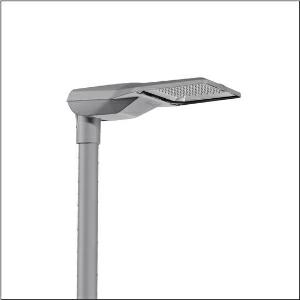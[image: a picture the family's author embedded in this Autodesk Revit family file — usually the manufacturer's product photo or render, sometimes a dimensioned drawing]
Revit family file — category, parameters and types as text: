
# Revit family: streetlight_sl_21_midi___st1_0a_5xe7d33a08nb_63de
name_source: partatom
category: Lighting Fixtures
units: mm (PartAtom-declared; Revit-internal decimal feet)

## family parameters
Cut with Voids When Loaded = No
Host = Face
Light Source = No
Part Type = Normal
Room Calculation Point = No
Round Connector Dimension = Use Diameter
Shared = No

## types (1)
- --- (1 x LED, 22700 lm, 151.2 W, 3000K)
    Apparent Load = 151 VA
    CIE Flux Codes = 40 73 97 100 100
    Color Rendering = 70
    Color Temperature = 3000K
    Default Elevation = 1800 mm
    Description = Streetlight SL 21 midi, mast luminaire, primary light control with lens, of PMMA, primary optical cover: cover, of toughened safety glass, transparent, light distribution: ST1.0a, light emission: direct distribution, primary light characteristic: asymmetric, installation type: post-top, side-entry, LED, 3G 1.5mm², High Power LED, rated luminous flux: 22.700lm, luminous efficacy: 150lm/W, light colour: 730, colour temperature: 3000K, control: flexible luminous flux parameterisation, time-dependent luminous flux control, constant luminous flux control, overheat protection, mains connection: 220..240V, AC, 50/60Hz, connection cable pre-assembled, cable length: 12,5m, wiring characteristics: H07RN-F, start of lifetime: 151W, end of service life: 157W, reduction: 70W, luminaire housing, of diecast aluminium, powder-coated, Siteco® metallic grey (DB 702S), corrosivity category C5 mid according to DIN EN ISO 12944, please order mast flange separately, inclination adjustable: 0°, 5°, 10°, 15°, sealing non-destructively replaceable, multi-level sealing system, length: 644mm, width: 335mm, height: 110mm, mast flange for spigot size: 42mm (side-entry): 5XC10008XM4, 60/48mm (side-entry/post-top): 5XC10108XM2, 76/60mm (side-entry/post-top): 5XC10108XM1, protection rating (complete): IP66, insulation class (complete): insulation class II (safety insulation), certification: CE, ENEC, ENEC+, VDE, impact resistance: IK09, permissible operating ambient temperature for outdoor applications: -40..+50°C, standard-compliant lighting for roads and squares, packaging unit: 1 piece

Light Distribution: ST1.0a
    Height = 111 mm
    Lamp = 1 x LED
    Lamp Light Flux = 22700 lm
    Lamp Power = 151.2 W
    Lamp count = 1
    Length = 644 mm
    Luminous efficacy = 150 lm/W
    Manufacturer = Siteco
    ModVariant = No
    Model = 5XE7D33A08NB
    Number of Poles = 1
    OnlyDefault = Yes
    Power Factor = 1
    Product Name = Streetlight SL 21 midi | ST1.0a
    Product group = mast luminaire | pylon top
    ProductGroupID = 6100
    Protection Class = Protection class II
    Protection Degree = IP 66
    RLX_Detail_Level = 1
    RLX_Emergency_Light_Flux = 0 lm
    RLX_Emergency_Type = 0
    RLX_Emergency_Type_DB = No
    RlxData = <blob elided: 90377 chars, md5=47859314>
    Socket = socket
    Standby Power = 0 W
    System Light Flux = 22700 lm
    System Power = 151 W
    Type Comments = factory setting: luminous flux: 100 % | Output Level: 100 % | 802 mA
    Type Image = l_1004298.jpg
    URL = http://relux.com
    VarID = @adj_103081
    Voltage = 0 V
    Weight = 0.00 kg
    Width = 336 mm

## geometry (parser evidence)
native form markers: Blend x4, Sweep x12
no freeform markers — native parametric forms only
